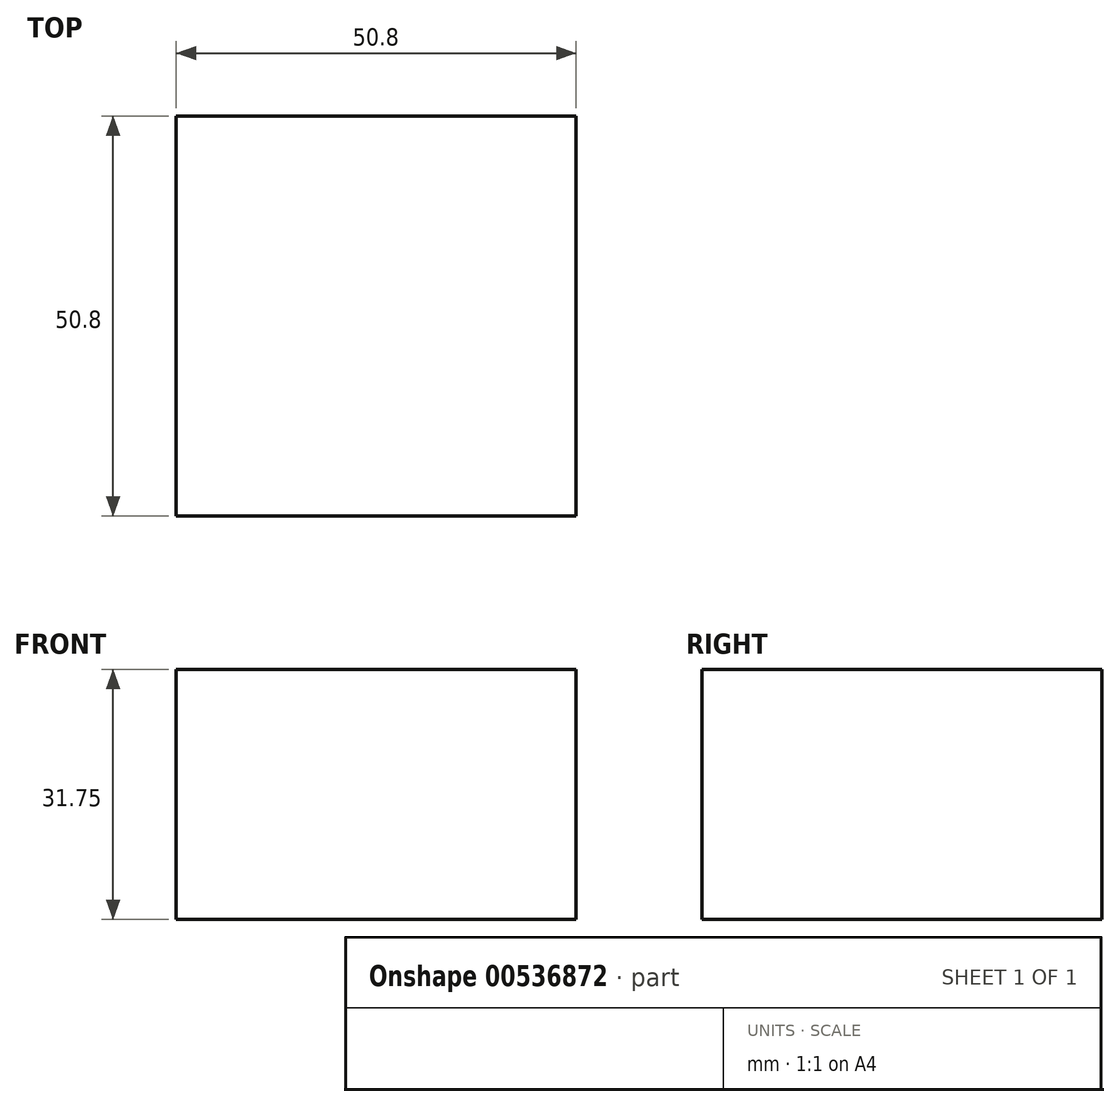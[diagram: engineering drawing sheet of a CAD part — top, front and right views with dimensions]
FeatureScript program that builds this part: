
annotation { "Feature Type Name" : "Feature", "Feature Type Description" : "" }
export const myFeature = defineFeature(function(context is Context, id is Id, definition is map)
    precondition{}
    {
        {
            var Q0;
            Q0=qCreatedBy(makeId("Top.planeOp"),FACE);
            var sketch = newSketch(context, id + "F0", { "sketchPlane" : qUnion([Q0])});
            skLineSegment(sketch, "E0.bottom", {"start": v(0, 0) * mm, "end": v(-50.8, 0) * mm});
            skLineSegment(sketch, "E0.top", {"start": v(0, 50.8) * mm, "end": v(-50.8, 50.8) * mm});
            skLineSegment(sketch, "E0.left", {"start": v(0, 0) * mm, "end": v(0, 50.8) * mm});
            skLineSegment(sketch, "E0.right", {"start": v(-50.8, 0) * mm, "end": v(-50.8, 50.8) * mm});
            skLineSegment(sketch, "E1.left", {"start": v(0, 50.8) * mm, "end": v(0, 50.8) * mm});
            skLineSegment(sketch, "E1.right", {"start": v(-50.8, 50.8) * mm, "end": v(-50.8, 50.8) * mm});
            skLineSegment(sketch, "E2.bottom", {"start": v(-50.8, 50.8) * mm, "end": v(0, 50.8) * mm});
            skLineSegment(sketch, "E2.top", {"start": v(-50.8, 50.8) * mm, "end": v(0, 50.8) * mm});
            skSolve(sketch);
        }
        {
            var Q0;
            Q0=makeQuery(id+"F0.imprint","IMPRINT",FACE,{"disambiguationData":[TD([[makeQuery(id+"F0.imprint","IMPRINT",EDGE,{"derivedFrom":sQuery(id+"F0.wireOp",EDGE,"E0.bottom")}),-1.0]])]});
            extrude(context, id + "F1", {"entities" : qUnion([Q0]), "depth" : 25.4 * mm, "offsetDistance" : 25.4 * mm});
        }
        {
            var Q0;
            Q0=makeQuery(id+"F1.opExtrude","CAP_FACE",FACE,{"disambiguationData":[OSD([sQuery(id+"F0.wireOp",EDGE,"E0.bottom"),sQuery(id+"F0.wireOp",EDGE,"E0.left"),sQuery(id+"F0.wireOp",EDGE,"E0.right"),sQuery(id+"F0.wireOp",EDGE,"E2.bottom")])],"isStart":false});
            extrude(context, id + "F2", {"entities" : qUnion([Q0]), "operationType" : NewBodyOperationType.ADD, "depth" : 6.35 * mm, "offsetDistance" : 25.4 * mm});
        }
        {
            var Q0;
            Q0 = qSketchRegion(id + "F0", true);
            var Q1;
            Q1 = qSketchRegion(id + "FPsEPQxWVa82KIn_0", true);
            extrude(context, id + "F3", {"entities" : qUnion([Q0, Q1]), "operationType" : NewBodyOperationType.ADD, "depth" : 20.83 * mm, "offsetDistance" : 25.4 * mm});
        }
    });
